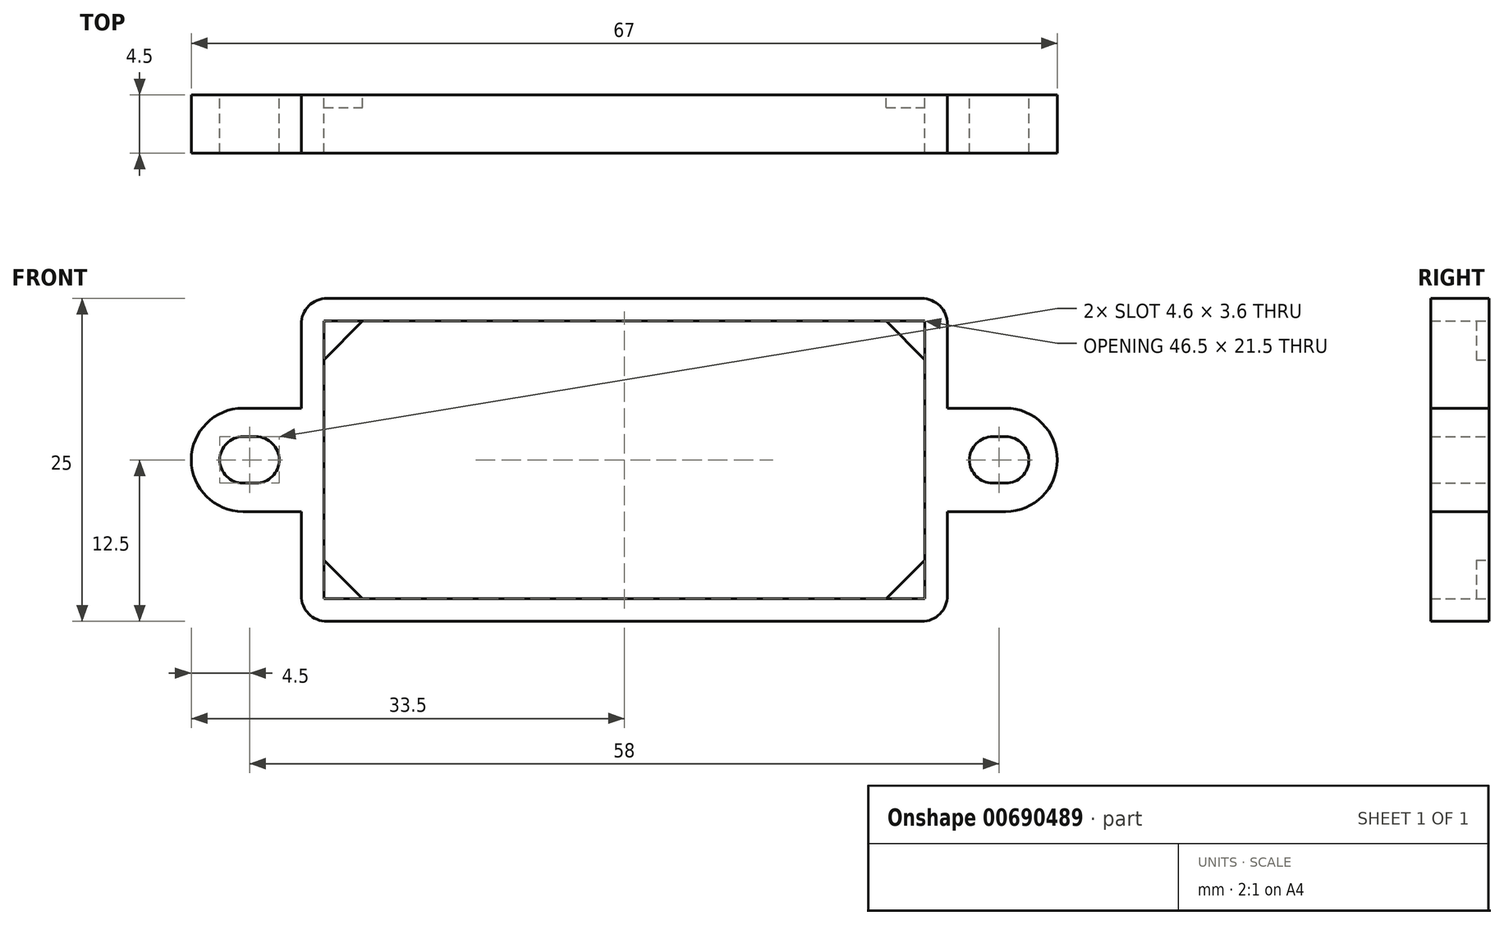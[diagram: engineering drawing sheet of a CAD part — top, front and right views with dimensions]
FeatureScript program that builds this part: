
annotation { "Feature Type Name" : "Feature", "Feature Type Description" : "" }
export const myFeature = defineFeature(function(context is Context, id is Id, definition is map)
    precondition{}
    {
        {
            var Q0;
            Q0=qCreatedBy(makeId("Front.planeOp"),FACE);
            var sketch = newSketch(context, id + "F0", { "sketchPlane" : qUnion([Q0])});
            skLineSegment(sketch, "E0.bottom", {"start": v(-23.25, 10.75) * mm, "end": v(23.25, 10.75) * mm});
            skLineSegment(sketch, "E0.top", {"start": v(-23.25, -10.75) * mm, "end": v(23.25, -10.75) * mm});
            skLineSegment(sketch, "E0.left", {"start": v(-23.25, 10.75) * mm, "end": v(-23.25, -10.75) * mm});
            skLineSegment(sketch, "E0.right", {"start": v(23.25, 10.75) * mm, "end": v(23.25, -10.75) * mm});
            skLineSegment(sketch, "E1.bottom", {"start": v(-25, 12.5) * mm, "end": v(25, 12.5) * mm});
            skLineSegment(sketch, "E1.top", {"start": v(-25, -12.5) * mm, "end": v(25, -12.5) * mm});
            skLineSegment(sketch, "E1.left", {"start": v(-25, 12.5) * mm, "end": v(-25, -12.5) * mm});
            skLineSegment(sketch, "E1.right", {"start": v(25, 12.5) * mm, "end": v(25, -12.5) * mm});
            skLineSegment(sketch, "E2", {"start": v(23.25, 7.75) * mm, "end": v(20.25, 10.75) * mm});
            skLineSegment(sketch, "E3.MirrorCS", {"start": v(23.25, -7.75) * mm, "end": v(20.25, -10.75) * mm});
            skLineSegment(sketch, "E4.MirrorCS", {"start": v(-23.25, 7.75) * mm, "end": v(-20.25, 10.75) * mm});
            skLineSegment(sketch, "E5.MirrorCS", {"start": v(-23.25, -7.75) * mm, "end": v(-20.25, -10.75) * mm});
            skLineSegment(sketch, "E6", {"start": v(-25, 4) * mm, "end": v(-29.5, 4) * mm});
            skLineSegment(sketch, "E7", {"start": v(-25, -4) * mm, "end": v(-29.5, -4) * mm});
            skArc(sketch, "E8", {"start": v(-29.5, 4) * mm, "mid": v(-33.5, 0) * mm, "end": v(-29.5, -4) * mm});
            skLineSegment(sketch, "E9.MirrorCS", {"start": v(25, 4) * mm, "end": v(29.5, 4) * mm});
            skLineSegment(sketch, "E10.MirrorCS", {"start": v(25, -4) * mm, "end": v(29.5, -4) * mm});
            skArc(sketch, "E11.MirrorCS", {"start": v(29.5, 4) * mm, "mid": v(33.5, 0) * mm, "end": v(29.5, -4) * mm});
            skLineSegment(sketch, "E12", {"start": v(-29.5, 0) * mm, "end": v(-28.5, 0) * mm, "construction": true});
            skArc(sketch, "E13.0.startCap", {"start": v(-29.5, -1.8) * mm, "mid": v(-31.3, 0) * mm, "end": v(-29.5, 1.8) * mm});
            skArc(sketch, "E13.0.endCap", {"start": v(-28.5, 1.8) * mm, "mid": v(-26.7, 0) * mm, "end": v(-28.5, -1.8) * mm});
            skLineSegment(sketch, "E13.0.left", {"start": v(-29.5, 1.8) * mm, "end": v(-28.5, 1.8) * mm});
            skLineSegment(sketch, "E13.0.right", {"start": v(-29.5, -1.8) * mm, "end": v(-28.5, -1.8) * mm});
            skLineSegment(sketch, "E14.MirrorCS", {"start": v(29.5, -1.8) * mm, "end": v(28.5, -1.8) * mm});
            skLineSegment(sketch, "E15.MirrorCS", {"start": v(29.5, 0) * mm, "end": v(28.5, 0) * mm, "construction": true});
            skLineSegment(sketch, "E16.MirrorCS", {"start": v(29.5, 1.8) * mm, "end": v(28.5, 1.8) * mm});
            skArc(sketch, "E17.MirrorCS", {"start": v(28.5, 1.8) * mm, "mid": v(26.7, 0) * mm, "end": v(28.5, -1.8) * mm});
            skArc(sketch, "E18.MirrorCS", {"start": v(29.5, -1.8) * mm, "mid": v(31.3, 0) * mm, "end": v(29.5, 1.8) * mm});
            skPoint(sketch, "E19", {"position": v(-29, 0) * mm});
            skPoint(sketch, "E20", {"position": v(29, 0) * mm});
            skSolve(sketch);
        }
        {
            var Q0;
            {var subQ20=sQuery(id+"F0.wireOp",EDGE,"E1.bottom");Q0=makeQuery(id+"F0.imprint","IMPRINT",FACE,{"disambiguationData":[TD([[makeQuery(id+"F0.imprint","IMPRINT",EDGE,{"derivedFrom":subQ20}),-1.0]])]});}
            var Q1;
            {var subQ3=sQuery(id+"F0.wireOp",EDGE,"E4.MirrorCS");Q1=makeQuery(id+"F0.imprint","IMPRINT",FACE,{"disambiguationData":[TD([[makeQuery(id+"F0.imprint","IMPRINT",EDGE,{"derivedFrom":subQ3}),1.0]])]});}
            var Q2;
            {var subQ3=sQuery(id+"F0.wireOp",EDGE,"E2");Q2=makeQuery(id+"F0.imprint","IMPRINT",FACE,{"disambiguationData":[TD([[makeQuery(id+"F0.imprint","IMPRINT",EDGE,{"derivedFrom":subQ3}),-1.0]])]});}
            var Q3;
            Q3=makeQuery(id+"F0.imprint","IMPRINT",FACE,{"disambiguationData":[TD([[makeQuery(id+"F0.imprint","IMPRINT",EDGE,{"derivedFrom":sQuery(id+"F0.wireOp",EDGE,"lAR11onk-Jfkd-lpEQ-tN8n-YO3bYSzZWp3R")}),-1.0]])]});
            var Q4;
            Q4=makeQuery(id+"F0.imprint","IMPRINT",FACE,{"disambiguationData":[TD([[makeQuery(id+"F0.imprint","IMPRINT",EDGE,{"derivedFrom":sQuery(id+"F0.wireOp",EDGE,"f9b12c6a-ef37-48fe-8d18-6f59947e3dd60.MirrorC")}),1.0]])]});
            var Q5;
            {var subQ0=sQuery(id+"F0.wireOp",EDGE,"E6");Q5=makeQuery(id+"F0.imprint","IMPRINT",FACE,{"disambiguationData":[TD([[makeQuery(id+"F0.imprint","IMPRINT",EDGE,{"derivedFrom":subQ0}),1.0]])]});}
            var Q6;
            {var subQ0=sQuery(id+"F0.wireOp",EDGE,"E9.MirrorCS");Q6=makeQuery(id+"F0.imprint","IMPRINT",FACE,{"disambiguationData":[TD([[makeQuery(id+"F0.imprint","IMPRINT",EDGE,{"derivedFrom":subQ0}),-1.0]])]});}
            extrude(context, id + "F1", {"entities" : qUnion([Q0, Q1, Q2, Q3, Q4, Q5, Q6]), "depth" : 4.5 * mm, "offsetDistance" : 25 * mm});
        }
        {
            var Q0;
            Q0=makeQuery(id+"F0.imprint","IMPRINT",FACE,{"disambiguationData":[TD([[makeQuery(id+"F0.imprint","IMPRINT",EDGE,{"derivedFrom":sQuery(id+"F0.wireOp",EDGE,"E0.bottom")}),-1.0]])]});
            extrude(context, id + "F2", {"entities" : qUnion([Q0]), "operationType" : NewBodyOperationType.REMOVE, "endBound" : BoundingType.THROUGH_ALL, "depth" : 3 * mm, "offsetDistance" : 25 * mm});
        }
        {
            var Q0;
            {var subQ3=sQuery(id+"F0.wireOp",EDGE,"E2");Q0=makeQuery(id+"F0.imprint","IMPRINT",FACE,{"disambiguationData":[TD([[makeQuery(id+"F0.imprint","IMPRINT",EDGE,{"derivedFrom":subQ3}),-1.0]])]});}
            var Q1;
            {var subQ3=sQuery(id+"F0.wireOp",EDGE,"E3.MirrorCS");Q1=makeQuery(id+"F0.imprint","IMPRINT",FACE,{"disambiguationData":[TD([[makeQuery(id+"F0.imprint","IMPRINT",EDGE,{"derivedFrom":subQ3}),1.0]])]});}
            var Q2;
            {var subQ3=sQuery(id+"F0.wireOp",EDGE,"E4.MirrorCS");Q2=makeQuery(id+"F0.imprint","IMPRINT",FACE,{"disambiguationData":[TD([[makeQuery(id+"F0.imprint","IMPRINT",EDGE,{"derivedFrom":subQ3}),1.0]])]});}
            var Q3;
            {var subQ3=sQuery(id+"F0.wireOp",EDGE,"E5.MirrorCS");Q3=makeQuery(id+"F0.imprint","IMPRINT",FACE,{"disambiguationData":[TD([[makeQuery(id+"F0.imprint","IMPRINT",EDGE,{"derivedFrom":subQ3}),-1.0]])]});}
            extrude(context, id + "F3", {"entities" : qUnion([Q0, Q1, Q2, Q3]), "operationType" : NewBodyOperationType.ADD, "depth" : 1 * mm, "offsetDistance" : 25 * mm});
        }
        {
            var Q0;
            Q0=makeQuery(id+"F1.opExtrude","SWEPT_EDGE",EDGE,{"disambiguationData":[OSD([sQuery(id+"F0.wireOp",EDGE,"E1.top"),sQuery(id+"F0.wireOp",EDGE,"E1.left")])]});
            var Q1;
            Q1=makeQuery(id+"F1.opExtrude","SWEPT_EDGE",EDGE,{"disambiguationData":[OSD([sQuery(id+"F0.wireOp",EDGE,"E1.top"),sQuery(id+"F0.wireOp",EDGE,"E1.right")])]});
            var Q2;
            Q2=makeQuery(id+"F1.opExtrude","SWEPT_EDGE",EDGE,{"disambiguationData":[OSD([sQuery(id+"F0.wireOp",EDGE,"E1.bottom"),sQuery(id+"F0.wireOp",EDGE,"E1.right")])]});
            var Q3;
            Q3=makeQuery(id+"F1.opExtrude","SWEPT_EDGE",EDGE,{"disambiguationData":[OSD([sQuery(id+"F0.wireOp",EDGE,"E1.bottom"),sQuery(id+"F0.wireOp",EDGE,"E1.left")])]});
            fillet(context, id + "F4", {"entities" : qUnion([Q0, Q1, Q2, Q3]), "radius" : 2 * mm, "tangentPropagation" : true, "allowEdgeOverflow" : false});
        }
    });
